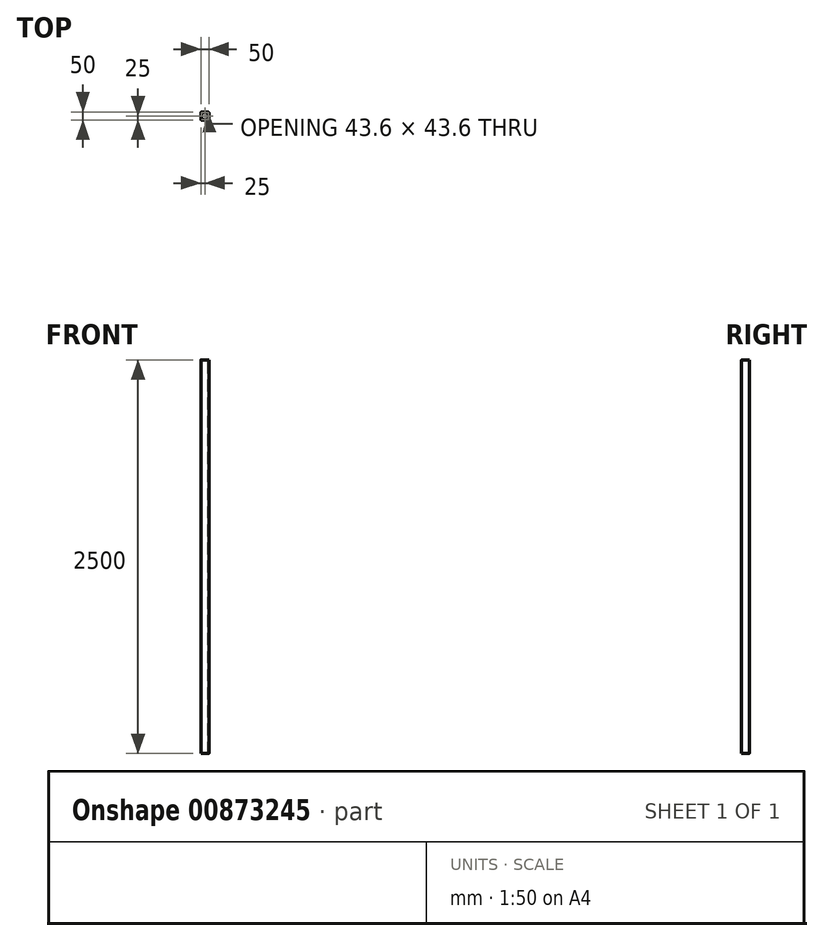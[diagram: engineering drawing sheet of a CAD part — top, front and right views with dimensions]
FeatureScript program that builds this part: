
annotation { "Feature Type Name" : "Feature", "Feature Type Description" : "" }
export const myFeature = defineFeature(function(context is Context, id is Id, definition is map)
    precondition{}
    {
        {
            var Q0;
            Q0=qCreatedBy(makeId("Top.planeOp"),FACE);
            var sketch = newSketch(context, id + "F0", { "sketchPlane" : qUnion([Q0])});
            skLineSegment(sketch, "E0.bottom", {"start": v(25, -25) * mm, "end": v(-25, -25) * mm});
            skLineSegment(sketch, "E0.top", {"start": v(25, 25) * mm, "end": v(-25, 25) * mm});
            skLineSegment(sketch, "E0.left", {"start": v(25, -25) * mm, "end": v(25, 25) * mm});
            skLineSegment(sketch, "E0.right", {"start": v(-25, -25) * mm, "end": v(-25, 25) * mm});
            skPoint(sketch, "E0.middle", {"position": v(0, 0) * mm});
            skSolve(sketch);
        }
        {
            var Q0;
            Q0=makeQuery(id+"F0.imprint","IMPRINT",FACE,{"disambiguationData":[TD([[makeQuery(id+"F0.imprint","IMPRINT",EDGE,{"derivedFrom":sQuery(id+"F0.wireOp",EDGE,"E0.bottom")}),-1.0]])]});
            extrude(context, id + "F1", {"entities" : qUnion([Q0]), "depth" : 2500 * mm, "offsetDistance" : 25 * mm});
        }
        {
            var Q0;
            Q0=makeQuery(id+"F1.opExtrude","CAP_FACE",FACE,{"disambiguationData":[OSD([sQuery(id+"F0.wireOp",EDGE,"E0.bottom"),sQuery(id+"F0.wireOp",EDGE,"E0.top"),sQuery(id+"F0.wireOp",EDGE,"E0.left"),sQuery(id+"F0.wireOp",EDGE,"E0.right")])],"isStart":false});
            var sketch = newSketch(context, id + "F2", { "sketchPlane" : qUnion([Q0])});
            skLineSegment(sketch, "E1.bottom", {"start": v(21.8, 21.8) * mm, "end": v(-21.8, 21.8) * mm});
            skLineSegment(sketch, "E1.top", {"start": v(21.8, -21.8) * mm, "end": v(-21.8, -21.8) * mm});
            skLineSegment(sketch, "E1.left", {"start": v(21.8, 21.8) * mm, "end": v(21.8, -21.8) * mm});
            skLineSegment(sketch, "E1.right", {"start": v(-21.8, 21.8) * mm, "end": v(-21.8, -21.8) * mm});
            skPoint(sketch, "E1.middle", {"position": v(0, 0) * mm});
            skSolve(sketch);
        }
        {
            var Q0;
            Q0=makeQuery(id+"F2.imprint","IMPRINT",FACE,{"disambiguationData":[TD([[makeQuery(id+"F2.imprint","IMPRINT",EDGE,{"derivedFrom":sQuery(id+"F2.wireOp",EDGE,"E1.bottom")}),1.0]])]});
            extrude(context, id + "F3", {"entities" : qUnion([Q0]), "operationType" : NewBodyOperationType.REMOVE, "endBound" : BoundingType.THROUGH_ALL, "oppositeDirection" : true, "depth" : 25 * mm, "offsetDistance" : 25 * mm});
        }
        {
            var Q0;
            Q0=makeQuery(id+"F1.opExtrude","SWEPT_EDGE",EDGE,{"disambiguationData":[OSD([sQuery(id+"F0.wireOp",EDGE,"E0.bottom"),sQuery(id+"F0.wireOp",EDGE,"E0.left")])]});
            var Q1;
            Q1=makeQuery(id+"F1.opExtrude","SWEPT_EDGE",EDGE,{"disambiguationData":[OSD([sQuery(id+"F0.wireOp",EDGE,"E0.top"),sQuery(id+"F0.wireOp",EDGE,"E0.left")])]});
            var Q2;
            Q2=makeQuery(id+"F1.opExtrude","SWEPT_EDGE",EDGE,{"disambiguationData":[OSD([sQuery(id+"F0.wireOp",EDGE,"E0.bottom"),sQuery(id+"F0.wireOp",EDGE,"E0.right")])]});
            var Q3;
            Q3=makeQuery(id+"F1.opExtrude","SWEPT_EDGE",EDGE,{"disambiguationData":[OSD([sQuery(id+"F0.wireOp",EDGE,"E0.top"),sQuery(id+"F0.wireOp",EDGE,"E0.right")])]});
            fillet(context, id + "F4", {"entities" : qUnion([Q0, Q1, Q2, Q3]), "radius" : 3 * mm, "tangentPropagation" : true, "allowEdgeOverflow" : false});
        }
        {
            var Q0;
            Q0=makeQuery(id+"F3.boolean.opBoolean","COPY",EDGE,{"derivedFrom":makeQuery(id+"F3.opExtrude","SWEPT_EDGE",EDGE,{"disambiguationData":[OSD([sQuery(id+"F2.wireOp",EDGE,"E1.top"),sQuery(id+"F2.wireOp",EDGE,"E1.left")])]})});
            var Q1;
            Q1=makeQuery(id+"F3.boolean.opBoolean","COPY",EDGE,{"derivedFrom":makeQuery(id+"F3.opExtrude","SWEPT_EDGE",EDGE,{"disambiguationData":[OSD([sQuery(id+"F2.wireOp",EDGE,"E1.bottom"),sQuery(id+"F2.wireOp",EDGE,"E1.right")])]})});
            var Q2;
            Q2=makeQuery(id+"F3.boolean.opBoolean","COPY",EDGE,{"derivedFrom":makeQuery(id+"F3.opExtrude","SWEPT_EDGE",EDGE,{"disambiguationData":[OSD([sQuery(id+"F2.wireOp",EDGE,"E1.bottom"),sQuery(id+"F2.wireOp",EDGE,"E1.left")])]})});
            var Q3;
            Q3=makeQuery(id+"F3.boolean.opBoolean","COPY",EDGE,{"derivedFrom":makeQuery(id+"F3.opExtrude","SWEPT_EDGE",EDGE,{"disambiguationData":[OSD([sQuery(id+"F2.wireOp",EDGE,"E1.top"),sQuery(id+"F2.wireOp",EDGE,"E1.right")])]})});
            fillet(context, id + "F5", {"entities" : qUnion([Q0, Q1, Q2, Q3]), "radius" : 1 * mm, "tangentPropagation" : true, "allowEdgeOverflow" : false});
        }
    });
